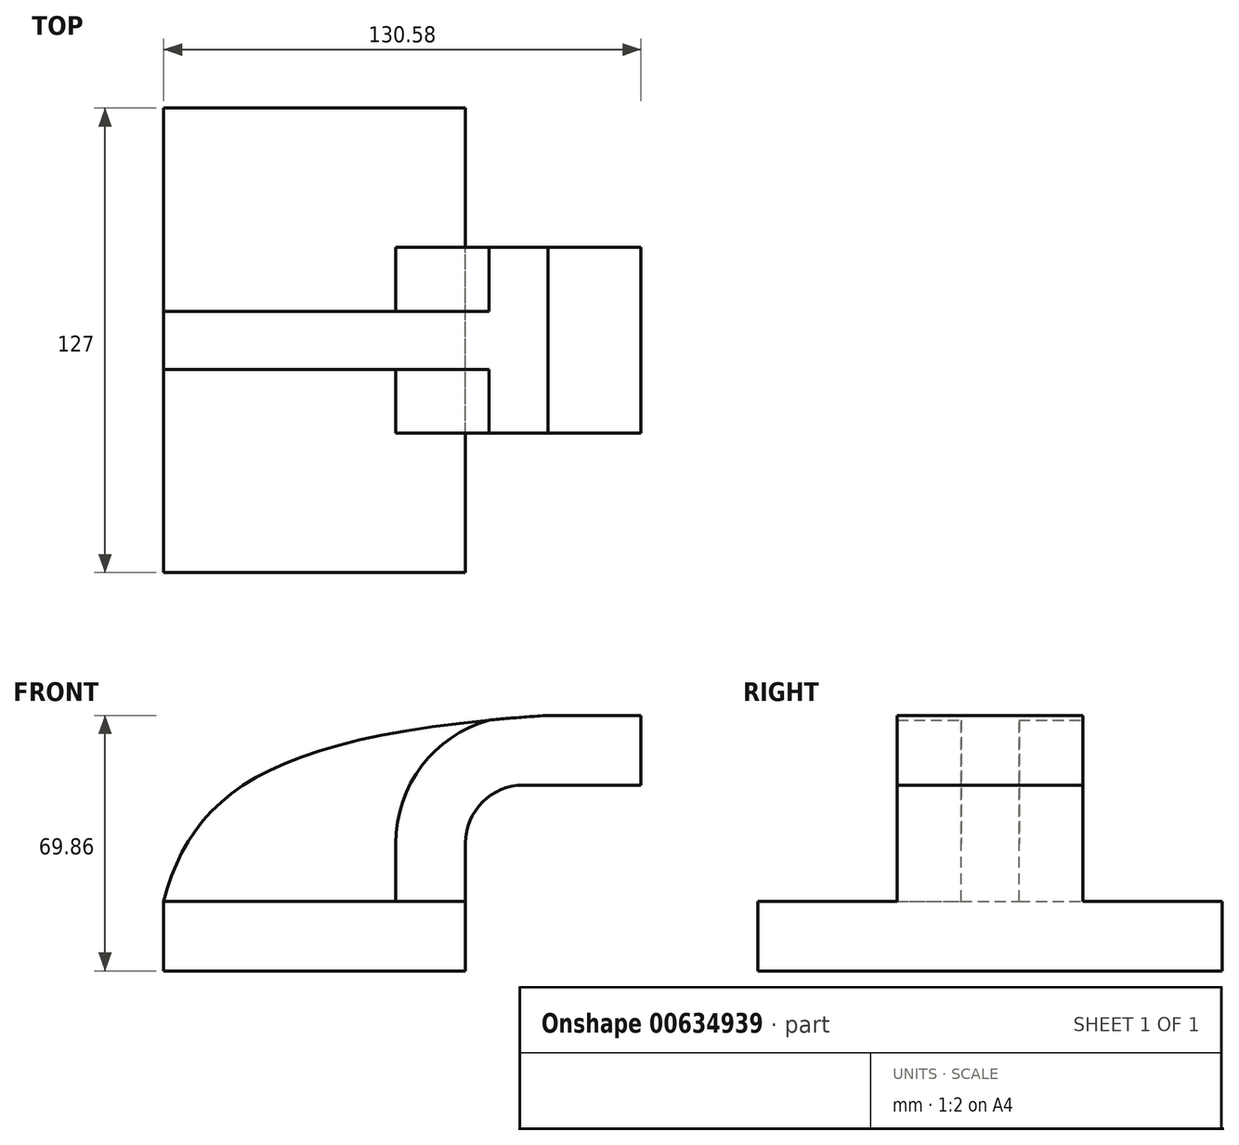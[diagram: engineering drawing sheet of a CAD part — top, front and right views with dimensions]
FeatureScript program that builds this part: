
annotation { "Feature Type Name" : "Feature", "Feature Type Description" : "" }
export const myFeature = defineFeature(function(context is Context, id is Id, definition is map)
    precondition{}
    {
        {
            var Q0;
            Q0=qCreatedBy(makeId("Front.planeOp"),FACE);
            var sketch = newSketch(context, id + "F0", { "sketchPlane" : qUnion([Q0])});
            skLineSegment(sketch, "E0.bottom", {"start": v(41.27, 9.53) * mm, "end": v(-41.28, 9.53) * mm});
            skLineSegment(sketch, "E0.top", {"start": v(41.28, -9.52) * mm, "end": v(-41.27, -9.53) * mm});
            skLineSegment(sketch, "E0.left", {"start": v(41.27, 9.53) * mm, "end": v(41.28, -9.52) * mm});
            skLineSegment(sketch, "E0.right", {"start": v(-41.28, 9.53) * mm, "end": v(-41.27, -9.53) * mm});
            skPoint(sketch, "E0.middle", {"position": v(0, 0) * mm});
            skLineSegment(sketch, "E1.bottom", {"start": v(114.7, 66.68) * mm, "end": v(63.9, 66.68) * mm});
            skLineSegment(sketch, "E1.top", {"start": v(114.7, 38.1) * mm, "end": v(63.9, 38.1) * mm});
            skLineSegment(sketch, "E1.left", {"start": v(114.7, 66.68) * mm, "end": v(114.7, 38.1) * mm});
            skLineSegment(sketch, "E1.right", {"start": v(63.9, 66.68) * mm, "end": v(63.9, 38.1) * mm});
            skPoint(sketch, "E1.middle", {"position": v(89.3, 52.39) * mm});
            skLineSegment(sketch, "E2", {"start": v(41.27, 9.53) * mm, "end": v(41.27, 25.4) * mm});
            skArc(sketch, "E3", {"start": v(41.27, 25.4) * mm, "mid": v(45.92, 36.63) * mm, "end": v(57.15, 41.27) * mm});
            skLineSegment(sketch, "E4", {"start": v(57.15, 41.27) * mm, "end": v(79.3, 41.27) * mm});
            skLineSegment(sketch, "E5.0", {"start": v(57.15, 60.33) * mm, "end": v(79.3, 60.33) * mm});
            skArc(sketch, "E5.1", {"start": v(22.22, 25.4) * mm, "mid": v(32.45, 50.1) * mm, "end": v(57.15, 60.32) * mm});
            skLineSegment(sketch, "E5.2", {"start": v(22.22, 9.53) * mm, "end": v(22.22, 25.4) * mm});
            skLineSegment(sketch, "E6", {"start": v(79.46, 38.1) * mm, "end": v(79.3, 66.68) * mm});
            skFitSpline(sketch, "E7", {"points": [v(-41.28, 9.53) * mm, v(63.9, 60.33) * mm], "startDerivative": vector(23.52, 88.99) * mm, "endDerivative": vector(229.48, 14.9) * mm});
            skSolve(sketch);
        }
        {
            var Q0;
            Q0=makeQuery(id+"F0.imprint","IMPRINT",FACE,{"disambiguationData":[TD([[makeQuery(id+"F0.imprint","IMPRINT",EDGE,{"derivedFrom":sQuery(id+"F0.wireOp",EDGE,"E0.top")}),-1.0]])]});
            extrude(context, id + "F1", {"entities" : qUnion([Q0]), "endBound" : BoundingType.SYMMETRIC, "depth" : 127 * mm, "offsetDistance" : 25.4 * mm});
        }
        {
            var Q0;
            {var subQ1=sQuery(id+"F0.wireOp",EDGE,"E2");Q0=makeQuery(id+"F0.imprint","IMPRINT",FACE,{"disambiguationData":[TD([[makeQuery(id+"F0.imprint","IMPRINT",EDGE,{"derivedFrom":subQ1}),1.0]])]});}
            extrude(context, id + "F2", {"entities" : qUnion([Q0]), "operationType" : NewBodyOperationType.ADD, "endBound" : BoundingType.SYMMETRIC, "depth" : 50.8 * mm, "offsetDistance" : 25.4 * mm});
        }
        {
            var Q0;
            {var subQ3=sQuery(id+"F0.wireOp",EDGE,"E5.2");Q0=makeQuery(id+"F0.imprint","IMPRINT",FACE,{"disambiguationData":[TD([[makeQuery(id+"F0.imprint","IMPRINT",EDGE,{"derivedFrom":subQ3}),1.0]])]});}
            extrude(context, id + "F3", {"entities" : qUnion([Q0]), "operationType" : NewBodyOperationType.ADD, "endBound" : BoundingType.SYMMETRIC, "depth" : 15.88 * mm, "offsetDistance" : 25.4 * mm});
        }
        {
            var Q0;
            Q0=makeQuery(id+"F2.opExtrude","SWEPT_FACE",FACE,{"disambiguationData":[OSD([sQuery(id+"F0.wireOp",EDGE,"E1.right")])]});
            extrude(context, id + "F4", {"entities" : qUnion([Q0]), "operationType" : NewBodyOperationType.ADD, "depth" : 25.4 * mm, "offsetDistance" : 25.4 * mm});
        }
    });
